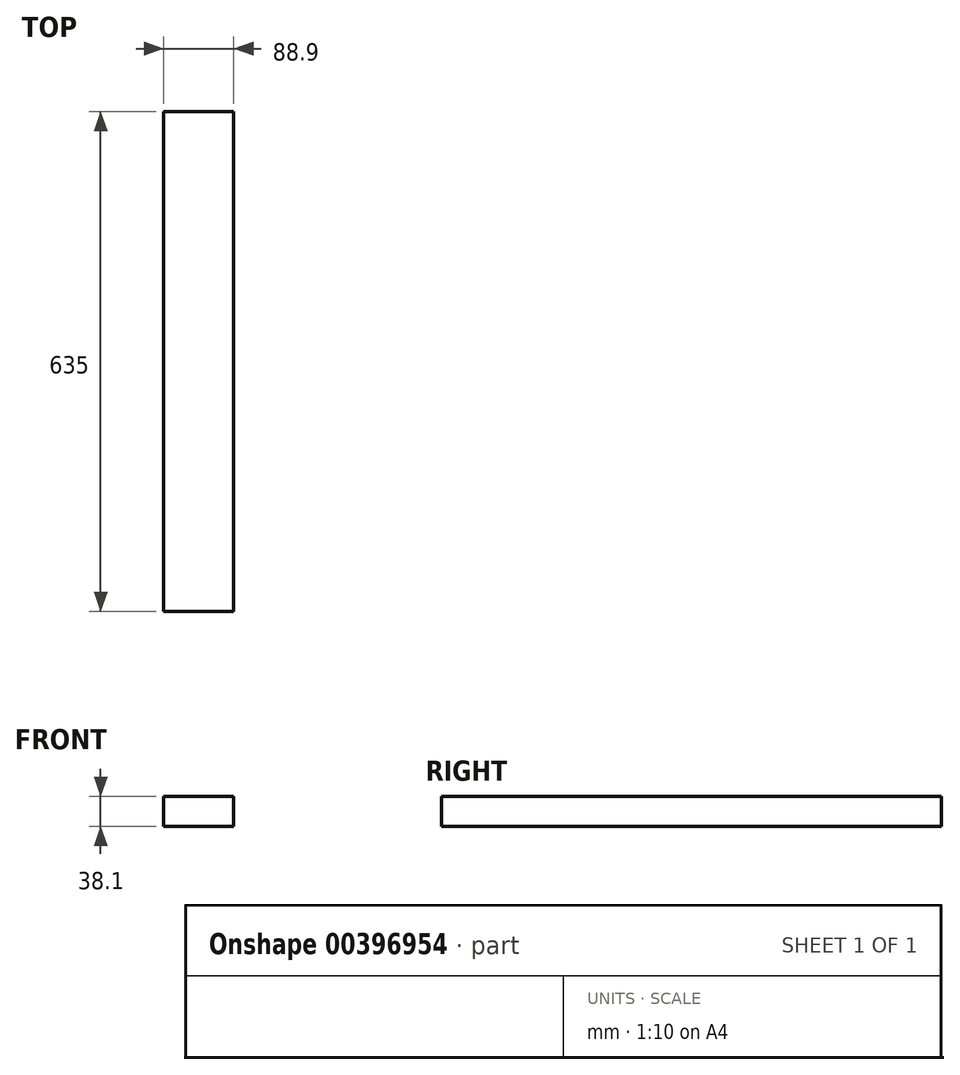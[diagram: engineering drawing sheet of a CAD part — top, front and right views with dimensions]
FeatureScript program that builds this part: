
annotation { "Feature Type Name" : "Feature", "Feature Type Description" : "" }
export const myFeature = defineFeature(function(context is Context, id is Id, definition is map)
    precondition{}
    {
        {
            var Q0;
            Q0=qCreatedBy(makeId("Front.planeOp"),FACE);
            var sketch = newSketch(context, id + "F0", { "sketchPlane" : qUnion([Q0])});
            skLineSegment(sketch, "E0.bottom", {"start": v(44.45, 19.05) * mm, "end": v(-44.45, 19.05) * mm});
            skLineSegment(sketch, "E0.top", {"start": v(44.45, -19.05) * mm, "end": v(-44.45, -19.05) * mm});
            skLineSegment(sketch, "E0.left", {"start": v(44.45, 19.05) * mm, "end": v(44.45, -19.05) * mm});
            skLineSegment(sketch, "E0.right", {"start": v(-44.45, 19.05) * mm, "end": v(-44.45, -19.05) * mm});
            skPoint(sketch, "E0.middle", {"position": v(0, 0) * mm});
            skSolve(sketch);
        }
        {
            var Q0;
            Q0=qSketchRegion(id+"F0",true);
            extrude(context, id + "F1", {"entities" : qUnion([Q0]), "depth" : 635 * mm});
        }
    });
